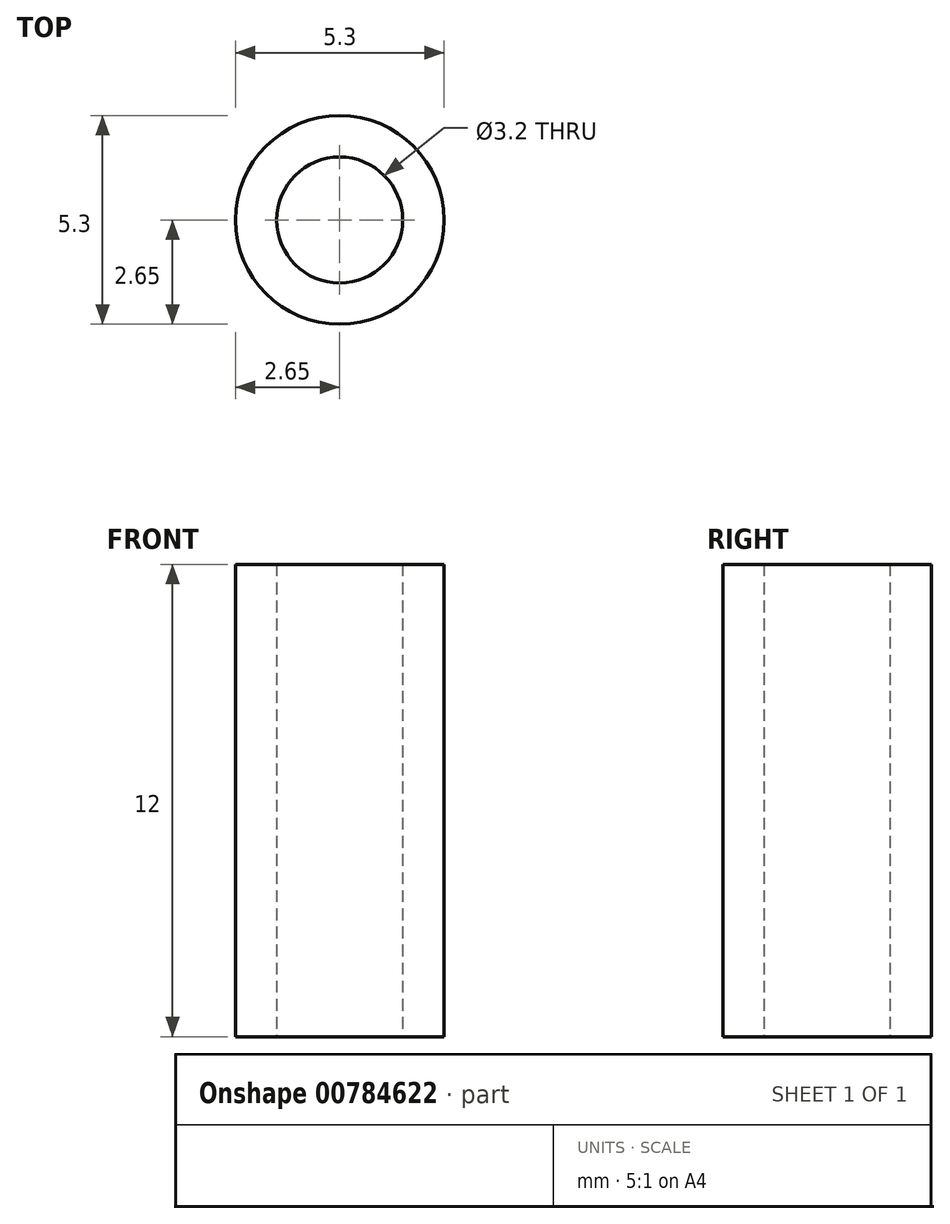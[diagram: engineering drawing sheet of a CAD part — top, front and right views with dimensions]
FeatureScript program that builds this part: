
annotation { "Feature Type Name" : "Feature", "Feature Type Description" : "" }
export const myFeature = defineFeature(function(context is Context, id is Id, definition is map)
    precondition{}
    {
        {
            var Q0;
            Q0=qCreatedBy(makeId("Top.planeOp"),FACE);
            var sketch = newSketch(context, id + "F0", { "sketchPlane" : qUnion([Q0])});
            skCircle(sketch, "E0", {"center": v(0, 0) * mm, "radius": 1.6 * mm});
            skCircle(sketch, "E1", {"center": v(0, 0) * mm, "radius": 2.65 * mm});
            skSolve(sketch);
        }
        {
            var Q0;
            Q0=makeQuery(id+"F0.imprint","IMPRINT",FACE,{"disambiguationData":[TD([[makeQuery(id+"F0.imprint","IMPRINT",EDGE,{"derivedFrom":sQuery(id+"F0.wireOp",EDGE,"E0")}),-1.0]])]});
            extrude(context, id + "F1", {"entities" : qUnion([Q0]), "depth" : 12 * mm, "offsetDistance" : 25 * mm});
        }
    });
